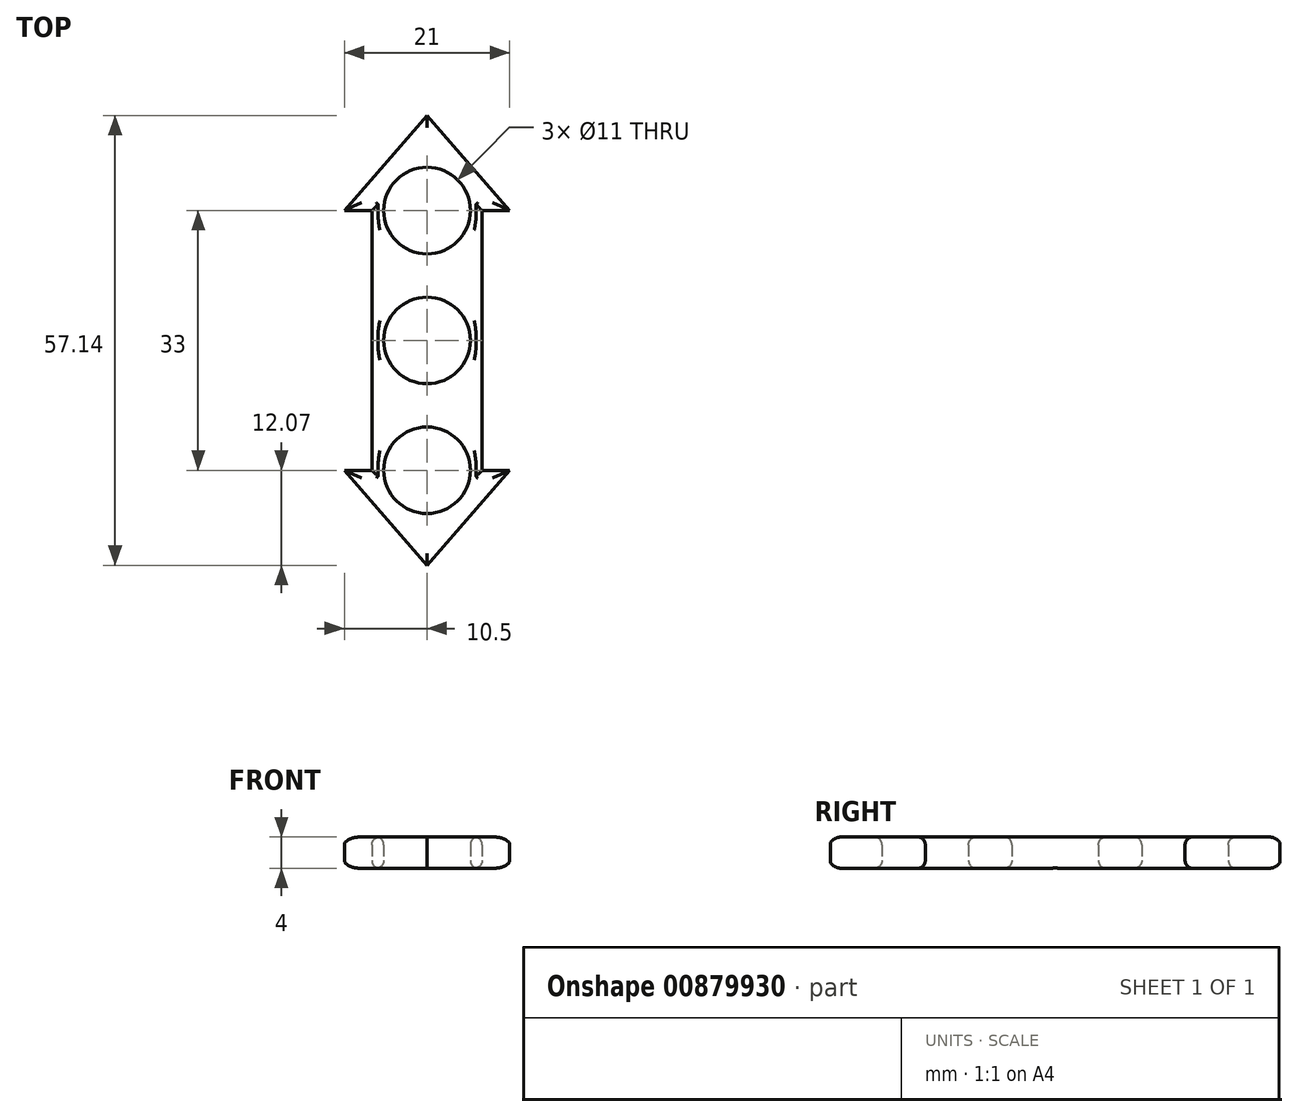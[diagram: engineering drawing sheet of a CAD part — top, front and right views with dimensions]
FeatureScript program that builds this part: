
annotation { "Feature Type Name" : "Feature", "Feature Type Description" : "" }
export const myFeature = defineFeature(function(context is Context, id is Id, definition is map)
    precondition{}
    {
        {
            var Q0;
            Q0=qCreatedBy(makeId("Top.planeOp"),FACE);
            var sketch = newSketch(context, id + "F0", { "sketchPlane" : qUnion([Q0])});
            skCircle(sketch, "E0", {"center": v(0, 0) * mm, "radius": 5.5 * mm});
            skLineSegment(sketch, "E1", {"start": v(0, 5.5) * mm, "end": v(0, 16.5) * mm, "construction": true});
            skLineSegment(sketch, "E2", {"start": v(-5.5, 16.5) * mm, "end": v(5.5, 16.5) * mm, "construction": true});
            skLineSegment(sketch, "E3", {"start": v(-3.5, 16.5) * mm, "end": v(-10.5, 16.5) * mm});
            skLineSegment(sketch, "E4", {"start": v(6, 16.5) * mm, "end": v(10.5, 16.5) * mm});
            skLineSegment(sketch, "E5", {"start": v(0, 16.5) * mm, "end": v(0, 28.57) * mm, "construction": true});
            skLineSegment(sketch, "E6.MirrorCS", {"start": v(-3.5, -16.5) * mm, "end": v(-10.5, -16.5) * mm});
            skLineSegment(sketch, "E7.MirrorCS", {"start": v(6, -16.5) * mm, "end": v(10.5, -16.5) * mm});
            skLineSegment(sketch, "E8.MirrorCS", {"start": v(0, -5.5) * mm, "end": v(0, -16.5) * mm, "construction": true});
            skLineSegment(sketch, "E9.MirrorCS", {"start": v(0, -16.5) * mm, "end": v(0, -28.57) * mm, "construction": true});
            skLineSegment(sketch, "E10", {"start": v(0, 28.57) * mm, "end": v(-10.5, 16.5) * mm});
            skPoint(sketch, "E11.MirrorCS.end.orphan", {"position": v(10.5, -16.5) * mm});
            skPoint(sketch, "E11.MirrorCS.start.orphan", {"position": v(0, -28.57) * mm});
            skLineSegment(sketch, "E12", {"start": v(0, 28.57) * mm, "end": v(10.5, 16.5) * mm});
            skLineSegment(sketch, "E13", {"start": v(10.5, -16.5) * mm, "end": v(0, -28.57) * mm});
            skPoint(sketch, "E14.MirrorCS.start.orphan", {"position": v(-10.5, -16.5) * mm});
            skLineSegment(sketch, "E15", {"start": v(-10.5, -16.5) * mm, "end": v(0, -28.57) * mm});
            skCircle(sketch, "E16", {"center": v(0, 16.5) * mm, "radius": 5.5 * mm});
            skCircle(sketch, "E17", {"center": v(0, -16.5) * mm, "radius": 5.5 * mm});
            skPoint(sketch, "E18.MirrorCS.end.orphan", {"position": v(-5.5, -16.5) * mm});
            skPoint(sketch, "E18.MirrorCS.start.orphan", {"position": v(-5.5, 0) * mm});
            skPoint(sketch, "E19.MirrorCS.end.orphan", {"position": v(5.5, -16.5) * mm});
            skPoint(sketch, "E19.MirrorCS.start.orphan", {"position": v(5.5, 0) * mm});
            skPoint(sketch, "E20.endSnap0", {"position": v(8, 16.5) * mm});
            skLineSegment(sketch, "E21", {"start": v(-7, 16.5) * mm, "end": v(-7, -16.5) * mm});
            skLineSegment(sketch, "E22", {"start": v(7, 16.5) * mm, "end": v(7, -16.5) * mm});
            skLineSegment(sketch, "E23", {"start": v(-10.5, -16.5) * mm, "end": v(10.5, -16.5) * mm, "construction": true});
            skSolve(sketch);
        }
        {
            var Q0;
            Q0=makeQuery(id+"F0.imprint","IMPRINT",FACE,{"disambiguationData":[TD([[makeQuery(id+"F0.imprint","IMPRINT",EDGE,{"derivedFrom":sQuery(id+"F0.wireOp",EDGE,"E0")}),-1.0]])]});
            extrude(context, id + "F1", {"entities" : qUnion([Q0]), "depth" : 4 * mm, "offsetDistance" : 25 * mm});
        }
        {
            var Q0;
            Q0=makeQuery(id+"F1.opExtrude","CAP_EDGE",EDGE,{"disambiguationData":[OSD([sQuery(id+"F0.wireOp",EDGE,"E21")])],"isStart":true});
            var Q1;
            Q1=makeQuery(id+"F1.opExtrude","CAP_EDGE",EDGE,{"disambiguationData":[OSD([sQuery(id+"F0.wireOp",EDGE,"E22")])],"isStart":true});
            var Q2;
            Q2=makeQuery(id+"F1.opExtrude","CAP_FACE",FACE,{"disambiguationData":[OSD([sQuery(id+"F0.wireOp",EDGE,"E0"),sQuery(id+"F0.wireOp",EDGE,"E3"),sQuery(id+"F0.wireOp",EDGE,"E4"),sQuery(id+"F0.wireOp",EDGE,"E6.MirrorCS"),sQuery(id+"F0.wireOp",EDGE,"E7.MirrorCS"),sQuery(id+"F0.wireOp",EDGE,"E10"),sQuery(id+"F0.wireOp",EDGE,"E12"),sQuery(id+"F0.wireOp",EDGE,"E13"),sQuery(id+"F0.wireOp",EDGE,"E15"),sQuery(id+"F0.wireOp",EDGE,"E16"),sQuery(id+"F0.wireOp",EDGE,"E17"),sQuery(id+"F0.wireOp",EDGE,"E21"),sQuery(id+"F0.wireOp",EDGE,"E22")])],"isStart":false});
            var Q3;
            Q3=makeQuery(id+"F1.opExtrude","CAP_FACE",FACE,{"disambiguationData":[OSD([sQuery(id+"F0.wireOp",EDGE,"E0"),sQuery(id+"F0.wireOp",EDGE,"E3"),sQuery(id+"F0.wireOp",EDGE,"E4"),sQuery(id+"F0.wireOp",EDGE,"E6.MirrorCS"),sQuery(id+"F0.wireOp",EDGE,"E7.MirrorCS"),sQuery(id+"F0.wireOp",EDGE,"E10"),sQuery(id+"F0.wireOp",EDGE,"E12"),sQuery(id+"F0.wireOp",EDGE,"E13"),sQuery(id+"F0.wireOp",EDGE,"E15"),sQuery(id+"F0.wireOp",EDGE,"E16"),sQuery(id+"F0.wireOp",EDGE,"E17"),sQuery(id+"F0.wireOp",EDGE,"E21"),sQuery(id+"F0.wireOp",EDGE,"E22")])],"isStart":true});
            var Q4;
            Q4=makeQuery(id+"F1.opExtrude","CAP_EDGE",EDGE,{"disambiguationData":[OSD([sQuery(id+"F0.wireOp",EDGE,"E16")])],"isStart":false});
            var Q5;
            Q5=makeQuery(id+"F1.opExtrude","CAP_EDGE",EDGE,{"disambiguationData":[OSD([sQuery(id+"F0.wireOp",EDGE,"E0")])],"isStart":false});
            var Q6;
            Q6=makeQuery(id+"F1.opExtrude","CAP_EDGE",EDGE,{"disambiguationData":[OSD([sQuery(id+"F0.wireOp",EDGE,"E17")])],"isStart":false});
            var Q7;
            Q7=makeQuery(id+"F1.opExtrude","CAP_EDGE",EDGE,{"disambiguationData":[OSD([sQuery(id+"F0.wireOp",EDGE,"E17")])],"isStart":true});
            var Q8;
            Q8=makeQuery(id+"F1.opExtrude","SWEPT_FACE",FACE,{"disambiguationData":[OSD([sQuery(id+"F0.wireOp",EDGE,"E0")])]});
            var Q9;
            Q9=makeQuery(id+"F1.opExtrude","CAP_EDGE",EDGE,{"disambiguationData":[OSD([sQuery(id+"F0.wireOp",EDGE,"E0")])],"isStart":true});
            var Q10;
            Q10=makeQuery(id+"F1.opExtrude","SWEPT_FACE",FACE,{"disambiguationData":[OSD([sQuery(id+"F0.wireOp",EDGE,"E16")])]});
            var Q11;
            Q11=makeQuery(id+"F1.opExtrude","CAP_EDGE",EDGE,{"disambiguationData":[OSD([sQuery(id+"F0.wireOp",EDGE,"E16")])],"isStart":true});
            fillet(context, id + "F2", {"entities" : qUnion([Q0, Q1, Q2, Q3, Q4, Q5, Q6, Q7, Q8, Q9, Q10, Q11]), "radius" : 1 * mm, "tangentPropagation" : true, "allowEdgeOverflow" : false});
        }
    });
